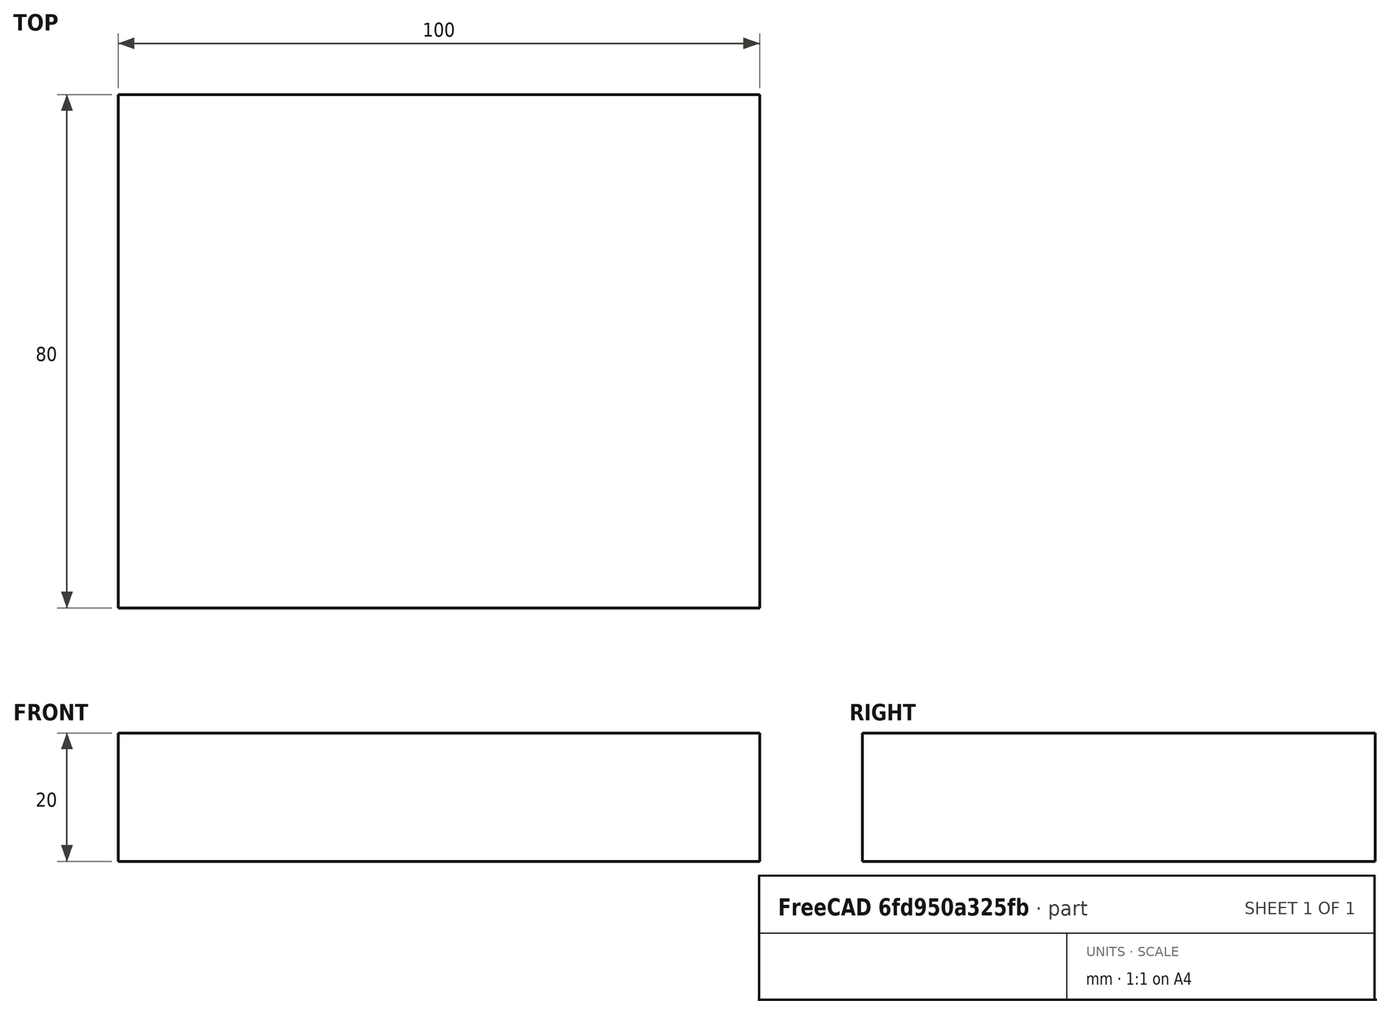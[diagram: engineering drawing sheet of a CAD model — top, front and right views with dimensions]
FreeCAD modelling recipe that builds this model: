
FCSTD DOCUMENT  (FreeCAD 0.18.4R)
Label: cannon-base
License: All rights reserved
LicenseURL: http://en.wikipedia.org/wiki/All_rights_reserved
objects: Sketcher::SketchObject×1, PartDesign::Pad×1, PartDesign::Body×1
note: 4 computed .brp shape members not serialized (recipe doc carries the construction recipe); baked Part::Feature solids carry a one-line shape summary decoded from their .brp

FEATURE [Sketcher::SketchObject] Sketch
  MapMode = 5
  Support = -> [XY_Plane]
  sketch-geometry (4):
    g0: LineSegment StartX=-50 StartY=40 StartZ=0 EndX=50 EndY=40 EndZ=0
    g1: LineSegment StartX=50 StartY=40 StartZ=0 EndX=50 EndY=-40 EndZ=0
    g2: LineSegment StartX=50 StartY=-40 StartZ=0 EndX=-50 EndY=-40 EndZ=0
    g3: LineSegment StartX=-50 StartY=-40 StartZ=0 EndX=-50 EndY=40 EndZ=0
  constraints (12):
    c: Coincident(g0,g1)
    c: Coincident(g1,g2)
    c: Coincident(g2,g3)
    c: Coincident(g3,g0)
    c: Horizontal(g0)
    c: Horizontal(g2)
    c: Vertical(g1)
    c: Vertical(g3)
    c: DistanceY(g3,g3) = 80
    c: DistanceY(g2,g-1) = 40
    c: DistanceX(g0,g0) = 100
    c: DistanceX(g0,g-1) = 50
FEATURE [PartDesign::Pad] Pad
  Length = 20
  Length2 = 100
  Midplane = true
  Profile = -> Sketch
  Type = 0
FEATURE [PartDesign::Body] Body
  Group = -> [Sketch,Pad]
  Origin = -> Origin
  Tip = -> Pad
